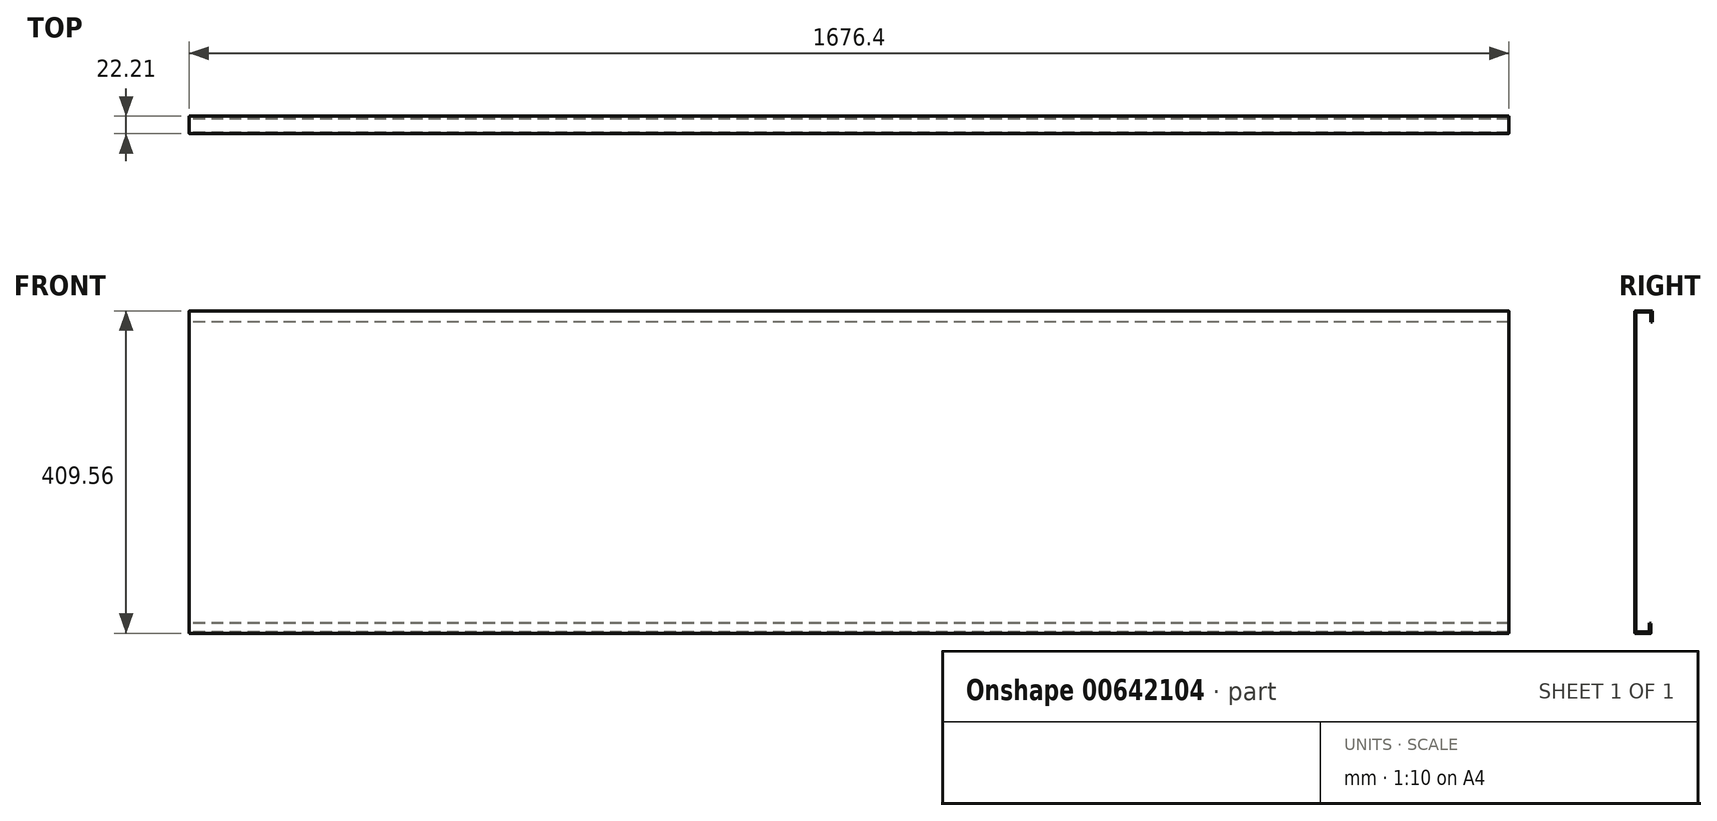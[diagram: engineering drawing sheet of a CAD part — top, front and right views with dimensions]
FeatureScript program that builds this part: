
annotation { "Feature Type Name" : "Feature", "Feature Type Description" : "" }
export const myFeature = defineFeature(function(context is Context, id is Id, definition is map)
    precondition{}
    {
        {
            var Q0;
            Q0=qCreatedBy(makeId("Right.planeOp"),FACE);
            var sketch = newSketch(context, id + "F0", { "sketchPlane" : qUnion([Q0])});
            skLineSegment(sketch, "E0.left", {"start": v(0.8, -202.82) * mm, "end": v(0.8, 202.82) * mm});
            skPoint(sketch, "E0.middle", {"position": v(0, 0) * mm});
            skLineSegment(sketch, "E1", {"start": v(1.17, 203.2) * mm, "end": v(19.46, 203.2) * mm});
            skLineSegment(sketch, "E2", {"start": v(19.84, 202.82) * mm, "end": v(19.84, 190.5) * mm});
            skLineSegment(sketch, "E3", {"start": v(-0.41, 204.77) * mm, "end": v(19.84, 204.77) * mm});
            skLineSegment(sketch, "E4", {"start": v(19.84, 204.77) * mm, "end": v(21.04, 204.77) * mm});
            skLineSegment(sketch, "E5", {"start": v(21.42, 204.4) * mm, "end": v(21.42, 190.5) * mm});
            skLineSegment(sketch, "E6", {"start": v(21.42, 190.5) * mm, "end": v(19.84, 190.5) * mm});
            skLineSegment(sketch, "E7", {"start": v(-0.8, 204.4) * mm, "end": v(-0.8, -203.2) * mm});
            skPoint(sketch, "E8.visualSharp", {"position": v(0.8, 203.2) * mm});
            skArc(sketch, "E8.filletArc", {"start": v(1.17, 203.2) * mm, "mid": v(0.9, 203.09) * mm, "end": v(0.8, 202.82) * mm});
            skPoint(sketch, "E9.visualSharp", {"position": v(19.84, 203.2) * mm});
            skArc(sketch, "E9.filletArc", {"start": v(19.84, 202.82) * mm, "mid": v(19.73, 203.09) * mm, "end": v(19.46, 203.2) * mm});
            skPoint(sketch, "E10.visualSharp", {"position": v(21.42, 204.77) * mm});
            skArc(sketch, "E10.filletArc", {"start": v(21.42, 204.4) * mm, "mid": v(21.3, 204.66) * mm, "end": v(21.04, 204.77) * mm});
            skPoint(sketch, "E11.visualSharp", {"position": v(-0.8, 204.77) * mm});
            skArc(sketch, "E11.filletArc", {"start": v(-0.41, 204.77) * mm, "mid": v(-0.68, 204.66) * mm, "end": v(-0.8, 204.4) * mm});
            skLineSegment(sketch, "E12", {"start": v(-0.8, -203.2) * mm, "end": v(-0.8, -204.4) * mm});
            skLineSegment(sketch, "E13", {"start": v(19.84, -204.4) * mm, "end": v(19.84, -192.1) * mm});
            skLineSegment(sketch, "E14", {"start": v(19.84, -192.1) * mm, "end": v(17.94, -191.92) * mm});
            skLineSegment(sketch, "E15", {"start": v(17.94, -191.92) * mm, "end": v(17.94, -202.82) * mm});
            skLineSegment(sketch, "E16", {"start": v(17.56, -203.2) * mm, "end": v(1.17, -203.2) * mm});
            skLineSegment(sketch, "E17", {"start": v(19.46, -204.79) * mm, "end": v(-0.41, -204.79) * mm});
            skPoint(sketch, "E18.visualSharp", {"position": v(17.94, -203.2) * mm});
            skArc(sketch, "E18.filletArc", {"start": v(17.56, -203.2) * mm, "mid": v(17.83, -203.09) * mm, "end": v(17.94, -202.82) * mm});
            skPoint(sketch, "E19.visualSharp", {"position": v(19.84, -204.79) * mm});
            skArc(sketch, "E19.filletArc", {"start": v(19.46, -204.79) * mm, "mid": v(19.73, -204.67) * mm, "end": v(19.84, -204.4) * mm});
            skPoint(sketch, "E20.visualSharp", {"position": v(-0.8, -204.79) * mm});
            skArc(sketch, "E20.filletArc", {"start": v(-0.8, -204.4) * mm, "mid": v(-0.68, -204.67) * mm, "end": v(-0.41, -204.79) * mm});
            skPoint(sketch, "E21.visualSharp", {"position": v(0.8, -203.2) * mm});
            skArc(sketch, "E21.filletArc", {"start": v(0.8, -202.82) * mm, "mid": v(0.9, -203.09) * mm, "end": v(1.17, -203.2) * mm});
            skSolve(sketch);
        }
        {
            var Q0;
            Q0=makeQuery(id+"F0.imprint","IMPRINT",FACE,{"disambiguationData":[TD([[makeQuery(id+"F0.imprint","IMPRINT",EDGE,{"derivedFrom":sQuery(id+"F0.wireOp",EDGE,"E0.left")}),1.0]])]});
            extrude(context, id + "F1", {"entities" : qUnion([Q0]), "depth" : 1676.4 * mm, "offsetDistance" : 25.4 * mm});
        }
    });
